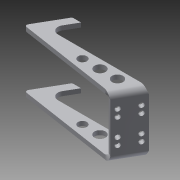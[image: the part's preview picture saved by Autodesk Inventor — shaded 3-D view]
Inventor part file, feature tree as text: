
AUTODESK INVENTOR PART (.ipt)
format: ipt  version: 2013 (Build 170138000, 138)  size: 1,845,760 bytes
history: native  units: in
note: dims shown in document units (in); Inventor stores cm internally (conversion verified against a paired STEP export)
features: sheet_metal_op x4, other x4, sketch x3, mirror x1
ambient origin geometry x8: Origin, YZ Plane, XZ Plane, XY Plane, X Axis, Y Axis, Z Axis, Center Point
bodies: Solid1 (feature_tree)
feature tree (12):
  sheet_metal_op  "Face1"
  sheet_metal_op  "Flange1"
  mirror  "Mirror1"
  sketch  "Sketch1"  dims[d0=0.625in]
  other  "Plate1"
  sketch  "Sketch2"  dims[d2=0.625in]
  other  "Plate2"
  sheet_metal_op  "Bend1"
  sheet_metal_op  "Corner1"
  sketch  "Sketch3"  dims[d3=0.5in d4=5.7114in d7=0.375in d8=0.125in d9=1.7657in d10=0.4278in d11=0.125in d12=0.4722in d13=60.0deg d14=0.7647in d15=1.0in d16=1.0in d17=1.0in d18=0.5in d19=1.6084in d20=0.5in d21=0.25in d22=0.25in d23=0.125in d24=0.5in d25=0.25in d26=1.75in d27=90.0deg d28=0.1in d29=1.0in d30=0.25in d31=0.25in d32=2.8in d33=0.266in d34=1.8in d35=1.6084in d36=0.3042in d37=0.7874in d39=1.8in d40=0.7874in d42=1.0in d45=0.25in d46=0.0in d47=0.266in d48=1.0in d49=0.3042in d50=0.7874in d52=1.0in d53=0.7874in d55=1.0in]
  other  "Cut1"
  other  "Definition1"
